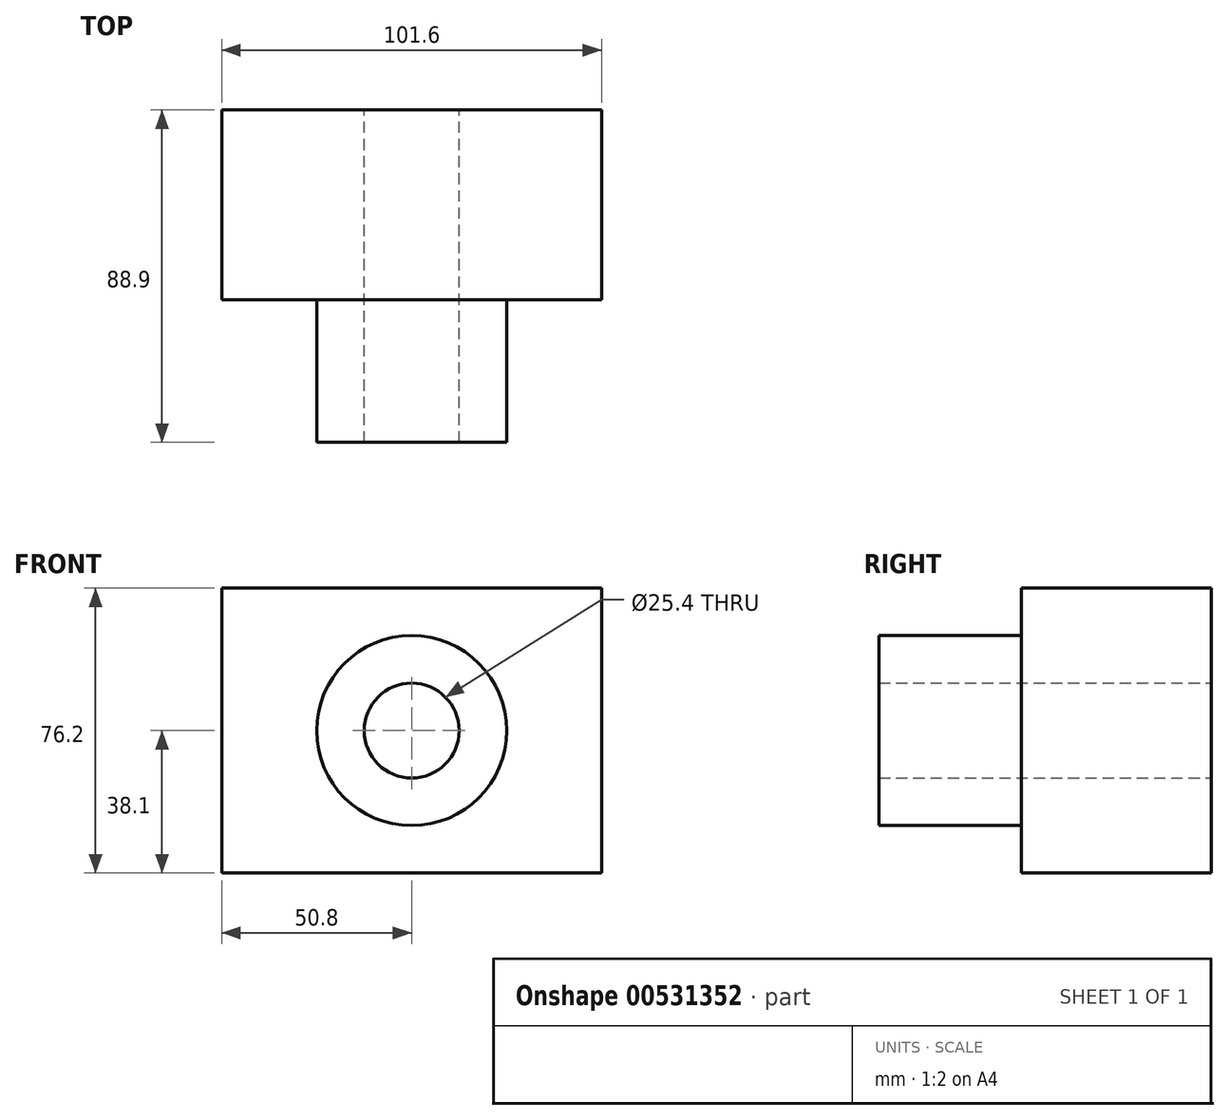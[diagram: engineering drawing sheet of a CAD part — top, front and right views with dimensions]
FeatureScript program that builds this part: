
annotation { "Feature Type Name" : "Feature", "Feature Type Description" : "" }
export const myFeature = defineFeature(function(context is Context, id is Id, definition is map)
    precondition{}
    {
        {
            var Q0;
            Q0=qCreatedBy(makeId("Front.planeOp"),FACE);
            var sketch = newSketch(context, id + "F0", { "sketchPlane" : qUnion([Q0])});
            skLineSegment(sketch, "E0.bottom", {"start": v(50.8, -38.1) * mm, "end": v(-50.8, -38.1) * mm});
            skLineSegment(sketch, "E0.top", {"start": v(50.8, 38.1) * mm, "end": v(-50.8, 38.1) * mm});
            skLineSegment(sketch, "E0.left", {"start": v(50.8, -38.1) * mm, "end": v(50.8, 38.1) * mm});
            skLineSegment(sketch, "E0.right", {"start": v(-50.8, -38.1) * mm, "end": v(-50.8, 38.1) * mm});
            skPoint(sketch, "E0.middle", {"position": v(0, 0) * mm});
            skSolve(sketch);
        }
        {
            var Q0;
            Q0=makeQuery(id+"F0.imprint","IMPRINT",FACE,{"disambiguationData":[TD([[makeQuery(id+"F0.imprint","IMPRINT",EDGE,{"derivedFrom":sQuery(id+"F0.wireOp",EDGE,"E0.bottom")}),-1.0]])]});
            extrude(context, id + "F1", {"entities" : qUnion([Q0]), "depth" : 50.8 * mm, "offsetDistance" : 25.4 * mm});
        }
        {
            var Q0;
            Q0=makeQuery(id+"F1.opExtrude","CAP_FACE",FACE,{"disambiguationData":[OSD([sQuery(id+"F0.wireOp",EDGE,"E0.bottom"),sQuery(id+"F0.wireOp",EDGE,"E0.top"),sQuery(id+"F0.wireOp",EDGE,"E0.left"),sQuery(id+"F0.wireOp",EDGE,"E0.right")])],"isStart":false});
            var sketch = newSketch(context, id + "F2", { "sketchPlane" : qUnion([Q0])});
            skCircle(sketch, "E1", {"center": v(0, 0) * mm, "radius": 25.4 * mm});
            skCircle(sketch, "E2", {"center": v(0, 0) * mm, "radius": 12.7 * mm});
            skSolve(sketch);
        }
        {
            var Q0;
            Q0=makeQuery(id+"F2.imprint","IMPRINT",FACE,{"disambiguationData":[TD([[makeQuery(id+"F2.imprint","IMPRINT",EDGE,{"derivedFrom":sQuery(id+"F2.wireOp",EDGE,"E1")}),1.0]])]});
            extrude(context, id + "F3", {"entities" : qUnion([Q0]), "operationType" : NewBodyOperationType.ADD, "depth" : 38.1 * mm, "offsetDistance" : 25.4 * mm});
        }
        {
            var Q0;
            Q0=makeQuery(id+"F3.boolean.opBoolean","SPLIT",FACE,{"disambiguationData":[TD([makeQuery(id+"F3.opExtrude","SWEPT_FACE",FACE,{"disambiguationData":[OSD([sQuery(id+"F2.wireOp",EDGE,"E2")])]})])],"derivedFrom":makeQuery(id+"F1.opExtrude","CAP_FACE",FACE,{"disambiguationData":[OSD([sQuery(id+"F0.wireOp",EDGE,"E0.bottom"),sQuery(id+"F0.wireOp",EDGE,"E0.top"),sQuery(id+"F0.wireOp",EDGE,"E0.left"),sQuery(id+"F0.wireOp",EDGE,"E0.right")])],"isStart":false})});
            extrude(context, id + "F4", {"entities" : qUnion([Q0]), "operationType" : NewBodyOperationType.REMOVE, "oppositeDirection" : true, "depth" : 88.65 * mm, "offsetDistance" : 25.4 * mm});
        }
    });
